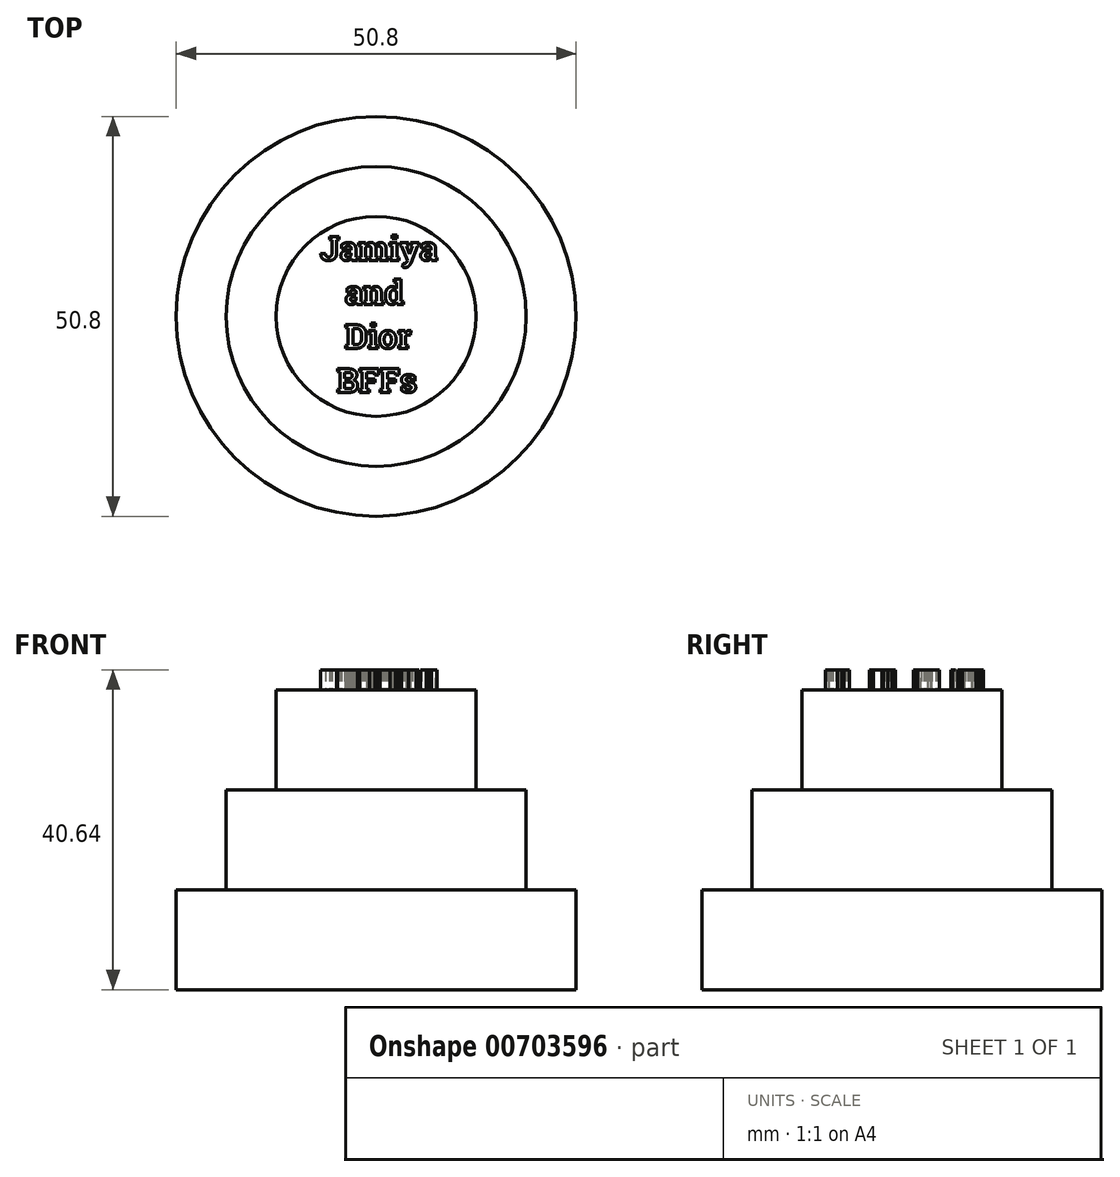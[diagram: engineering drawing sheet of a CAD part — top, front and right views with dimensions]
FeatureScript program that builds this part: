
annotation { "Feature Type Name" : "Feature", "Feature Type Description" : "" }
export const myFeature = defineFeature(function(context is Context, id is Id, definition is map)
    precondition{}
    {
        {
            var Q0;
            Q0=qCreatedBy(makeId("Front.planeOp"),FACE);
            var sketch = newSketch(context, id + "F0", { "sketchPlane" : qUnion([Q0])});
            skLineSegment(sketch, "E0.bottom", {"start": v(0, 0) * mm, "end": v(25.4, 0) * mm});
            skLineSegment(sketch, "E0.top", {"start": v(0, 12.7) * mm, "end": v(25.4, 12.7) * mm});
            skLineSegment(sketch, "E0.left", {"start": v(0, 0) * mm, "end": v(0, 12.7) * mm});
            skLineSegment(sketch, "E0.right", {"start": v(25.4, 0) * mm, "end": v(25.4, 12.7) * mm});
            skSolve(sketch);
        }
        {
            var Q0;
            Q0=makeQuery(id+"F0.imprint","IMPRINT",FACE,{"disambiguationData":[TD([[makeQuery(id+"F0.imprint","IMPRINT",EDGE,{"derivedFrom":sQuery(id+"F0.wireOp",EDGE,"E0.bottom")}),1.0]])]});
            var Q1;
            Q1=sQuery(id+"F0.wireOp",EDGE,"E0.left");
            revolve(context, id + "F1", {"surfaceOperationType" : NewSurfaceOperationType.NEW, "entities" : qUnion([Q0]), "axis" : qUnion([Q1]), "revolveType" : RevolveType.FULL});
        }
        {
            var Q0;
            Q0=makeQuery(id+"F1.opRevolve","SWEPT_FACE",FACE,{"disambiguationData":[OSD([sQuery(id+"F0.wireOp",EDGE,"E0.top")])]});
            var sketch = newSketch(context, id + "F2", { "sketchPlane" : qUnion([Q0])});
            skCircle(sketch, "E1", {"center": v(0, 0) * mm, "radius": 19.05 * mm});
            skSolve(sketch);
        }
        {
            var Q0;
            Q0=makeQuery(id+"F2.imprint","IMPRINT",FACE,{"disambiguationData":[TD([[makeQuery(id+"F2.imprint","IMPRINT",EDGE,{"derivedFrom":sQuery(id+"F2.wireOp",EDGE,"E1")}),1.0]])]});
            extrude(context, id + "F3", {"entities" : qUnion([Q0]), "operationType" : NewBodyOperationType.ADD, "depth" : 12.7 * mm, "offsetDistance" : 25.4 * mm});
        }
        {
            var Q0;
            Q0=makeQuery(id+"F3.opExtrude","CAP_FACE",FACE,{"disambiguationData":[OSD([sQuery(id+"F2.wireOp",EDGE,"E1")])],"isStart":false});
            var sketch = newSketch(context, id + "F4", { "sketchPlane" : qUnion([Q0])});
            skCircle(sketch, "E2", {"center": v(0, 0) * mm, "radius": 12.7 * mm});
            skSolve(sketch);
        }
        {
            var Q0;
            Q0=makeQuery(id+"F4.imprint","IMPRINT",FACE,{"disambiguationData":[TD([[makeQuery(id+"F4.imprint","IMPRINT",EDGE,{"derivedFrom":sQuery(id+"F4.wireOp",EDGE,"E2")}),1.0]])]});
            extrude(context, id + "F5", {"entities" : qUnion([Q0]), "operationType" : NewBodyOperationType.ADD, "depth" : 12.7 * mm, "offsetDistance" : 25.4 * mm});
        }
        {
            var Q0;
            Q0=makeQuery(id+"F5.opExtrude","CAP_FACE",FACE,{"disambiguationData":[OSD([sQuery(id+"F4.wireOp",EDGE,"E2")])],"isStart":false});
            var sketch = newSketch(context, id + "F6", { "sketchPlane" : qUnion([Q0])});
            skText(sketch, "E3", { "text": "Jamiya\n   and\n   Dior\n  BFFs", "fontName": "RobotoSlab-Bold.ttf"});
            const initialGuessF6  = {"E3": [-0.00711, 0.00711, 1, 0, 0.00305]};
            skSetInitialGuess(sketch, initialGuessF6);
            skSolve(sketch);
        }
        {
            var Q0;
            Q0 = qSketchRegion(id + "F6", true);
            extrude(context, id + "F7", {"entities" : qUnion([Q0]), "operationType" : NewBodyOperationType.ADD, "depth" : 2.54 * mm, "offsetDistance" : 25.4 * mm});
        }
    });
